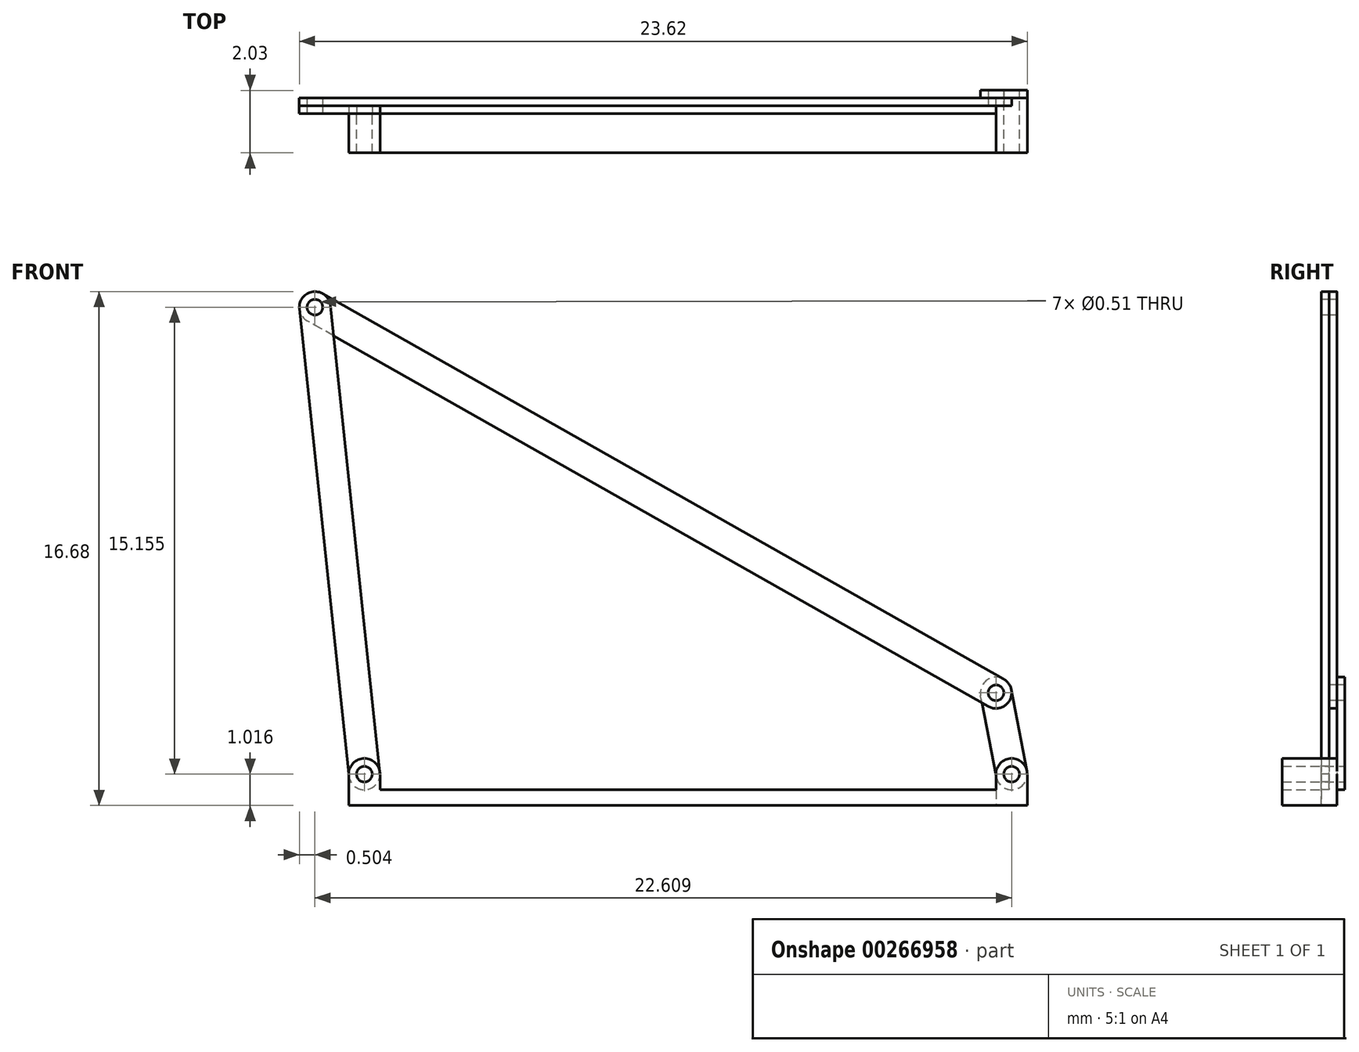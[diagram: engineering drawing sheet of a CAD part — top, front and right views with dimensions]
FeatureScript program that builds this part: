
annotation { "Feature Type Name" : "Feature", "Feature Type Description" : "" }
export const myFeature = defineFeature(function(context is Context, id is Id, definition is map)
    precondition{}
    {
        {
            var Q0;
            Q0=qCreatedBy(makeId("Front.planeOp"),FACE);
            var sketch = newSketch(context, id + "F0", { "sketchPlane" : qUnion([Q0])});
            skLineSegment(sketch, "E0.bottom", {"start": v(0, 0) * mm, "end": v(22.02, 0) * mm});
            skLineSegment(sketch, "E0.top", {"start": v(0, 0.5) * mm, "end": v(22.02, 0.5) * mm});
            skLineSegment(sketch, "E0.left", {"start": v(0, 0) * mm, "end": v(0, 0.5) * mm});
            skLineSegment(sketch, "E0.right", {"start": v(22.02, 0) * mm, "end": v(22.02, 0.5) * mm});
            skArc(sketch, "E1", {"start": v(1.02, 1.02) * mm, "mid": v(0.5, 1.52) * mm, "end": v(0, 1.02) * mm});
            skCircle(sketch, "E2", {"center": v(0.5, 1.02) * mm, "radius": 0.25 * mm});
            skLineSegment(sketch, "E3", {"start": v(0, 0.5) * mm, "end": v(0, 1.36) * mm});
            skLineSegment(sketch, "E4", {"start": v(1.02, 1.02) * mm, "end": v(1.02, 0.5) * mm});
            skArc(sketch, "E5", {"start": v(22.02, 1.02) * mm, "mid": v(21.51, 1.52) * mm, "end": v(21, 1.02) * mm});
            skCircle(sketch, "E6", {"center": v(21.51, 1.02) * mm, "radius": 0.25 * mm});
            skLineSegment(sketch, "E7", {"start": v(22.02, 1.02) * mm, "end": v(22.02, 0.5) * mm});
            skLineSegment(sketch, "E8", {"start": v(21, 1.02) * mm, "end": v(21, 0.5) * mm});
            skLineSegment(sketch, "E9", {"start": v(2.53, 4.51) * mm, "end": v(23.12, 16.17) * mm, "construction": true});
            skLineSegment(sketch, "E10", {"start": v(23.12, 16.17) * mm, "end": v(21.51, 1.02) * mm, "construction": true});
            skLineSegment(sketch, "E11", {"start": v(0.5, 1.02) * mm, "end": v(2.53, 4.51) * mm, "construction": true});
            skSolve(sketch);
        }
        {
            var Q0;
            {var subQ3=sQuery(id+"F0.wireOp",EDGE,"E1");Q0=makeQuery(id+"F0.imprint","IMPRINT",FACE,{"disambiguationData":[TD([[makeQuery(id+"F0.imprint","IMPRINT",EDGE,{"derivedFrom":subQ3}),1.0]])]});}
            var Q1;
            Q1=makeQuery(id+"F0.imprint","IMPRINT",FACE,{"disambiguationData":[TD([[makeQuery(id+"F0.imprint","IMPRINT",EDGE,{"derivedFrom":sQuery(id+"F0.wireOp",EDGE,"E0.bottom")}),1.0]])]});
            var Q2;
            Q2=makeQuery(id+"F0.imprint","IMPRINT",FACE,{"disambiguationData":[TD([[makeQuery(id+"F0.imprint","IMPRINT",EDGE,{"derivedFrom":sQuery(id+"F0.wireOp",EDGE,"E5")}),1.0]])]});
            extrude(context, id + "F1", {"entities" : qUnion([Q0, Q1, Q2]), "depth" : 1.27 * mm});
        }
        {
            var Q0;
            Q0=makeQuery(id+"F1.opExtrude","CAP_FACE",FACE,{"disambiguationData":[OSD([sQuery(id+"F0.wireOp",EDGE,"E0.bottom"),sQuery(id+"F0.wireOp",EDGE,"E0.top"),sQuery(id+"F0.wireOp",EDGE,"E0.left"),sQuery(id+"F0.wireOp",EDGE,"E0.right"),sQuery(id+"F0.wireOp",EDGE,"E1"),sQuery(id+"F0.wireOp",EDGE,"E2"),sQuery(id+"F0.wireOp",EDGE,"E3"),sQuery(id+"F0.wireOp",EDGE,"E4"),sQuery(id+"F0.wireOp",EDGE,"E5"),sQuery(id+"F0.wireOp",EDGE,"E6"),sQuery(id+"F0.wireOp",EDGE,"E7"),sQuery(id+"F0.wireOp",EDGE,"E8")])],"isStart":true});
            var sketch = newSketch(context, id + "F2", { "sketchPlane" : qUnion([Q0])});
            skCircle(sketch, "E12.0", {"center": v(-0.5, 1.02) * mm, "radius": 0.25 * mm});
            skCircle(sketch, "E13", {"center": v(-0.5, 1.02) * mm, "radius": 0.5 * mm});
            skLineSegment(sketch, "E14", {"start": v(-0.5, 1.02) * mm, "end": v(1.1, 16.17) * mm, "construction": true});
            skCircle(sketch, "E15", {"center": v(1.1, 16.17) * mm, "radius": 0.5 * mm});
            skLineSegment(sketch, "E16", {"start": v(0.6, 16.22) * mm, "end": v(-1.01, 1.07) * mm});
            skLineSegment(sketch, "E17", {"start": v(1.6, 16.12) * mm, "end": v(0, 1.02) * mm});
            skCircle(sketch, "E18", {"center": v(1.1, 16.17) * mm, "radius": 0.25 * mm});
            skSolve(sketch);
        }
        {
            var Q0;
            Q0 = qSketchRegion(id + "F2", true);
            extrude(context, id + "F3", {"entities" : qUnion([Q0]), "depth" : 0.25 * mm});
        }
        {
            var Q0;
            Q0=makeQuery(id+"F3.opExtrude","CAP_FACE",FACE,{"disambiguationData":[OSD([sQuery(id+"F2.wireOp",EDGE,"E12.0"),sQuery(id+"F2.wireOp",EDGE,"E13"),sQuery(id+"F2.wireOp",EDGE,"E15"),sQuery(id+"F2.wireOp",EDGE,"E16"),sQuery(id+"F2.wireOp",EDGE,"E17"),sQuery(id+"F2.wireOp",EDGE,"E18")])],"isStart":false});
            var sketch = newSketch(context, id + "F4", { "sketchPlane" : qUnion([Q0])});
            skCircle(sketch, "E19.0", {"center": v(1.1, 16.17) * mm, "radius": 0.25 * mm});
            skCircle(sketch, "E20", {"center": v(1.1, 16.17) * mm, "radius": 0.5 * mm});
            skLineSegment(sketch, "E21", {"start": v(1.1, 16.17) * mm, "end": v(-21, 3.66) * mm, "construction": true});
            skCircle(sketch, "E22", {"center": v(-21, 3.66) * mm, "radius": 0.5 * mm});
            skCircle(sketch, "E23", {"center": v(-21, 3.66) * mm, "radius": 0.25 * mm});
            skLineSegment(sketch, "E24", {"start": v(-21.26, 4.1) * mm, "end": v(0.85, 16.61) * mm});
            skLineSegment(sketch, "E25", {"start": v(-20.76, 3.21) * mm, "end": v(1.35, 15.73) * mm});
            skSolve(sketch);
        }
        {
            var Q0;
            Q0 = qSketchRegion(id + "F4", true);
            extrude(context, id + "F5", {"entities" : qUnion([Q0]), "depth" : 0.25 * mm});
        }
        {
            var Q0;
            Q0=makeQuery(id+"F5.opExtrude","CAP_FACE",FACE,{"disambiguationData":[OSD([sQuery(id+"F4.wireOp",EDGE,"E19.0"),sQuery(id+"F4.wireOp",EDGE,"E20"),sQuery(id+"F4.wireOp",EDGE,"E22"),sQuery(id+"F4.wireOp",EDGE,"E23"),sQuery(id+"F4.wireOp",EDGE,"E24"),sQuery(id+"F4.wireOp",EDGE,"E25")])],"isStart":false});
            var sketch = newSketch(context, id + "F6", { "sketchPlane" : qUnion([Q0])});
            skCircle(sketch, "E26.0", {"center": v(-21, 3.66) * mm, "radius": 0.25 * mm});
            skCircle(sketch, "E27.0", {"center": v(-21.51, 1.02) * mm, "radius": 0.25 * mm});
            skCircle(sketch, "E28", {"center": v(-21, 3.66) * mm, "radius": 0.5 * mm});
            skCircle(sketch, "E29", {"center": v(-21.51, 1.02) * mm, "radius": 0.5 * mm});
            skLineSegment(sketch, "E30", {"start": v(-22.01, 1.11) * mm, "end": v(-21.5, 3.75) * mm});
            skLineSegment(sketch, "E31", {"start": v(-21.01, 0.92) * mm, "end": v(-20.5, 3.56) * mm});
            skSolve(sketch);
        }
        {
            var Q0;
            Q0 = qSketchRegion(id + "F6", true);
            extrude(context, id + "F7", {"entities" : qUnion([Q0]), "depth" : 0.25 * mm});
        }
        {
            var Q0;
            Q0=makeQuery(id+"F1.opExtrude","CAP_FACE",FACE,{"disambiguationData":[OSD([sQuery(id+"F0.wireOp",EDGE,"E0.bottom"),sQuery(id+"F0.wireOp",EDGE,"E0.top"),sQuery(id+"F0.wireOp",EDGE,"E0.left"),sQuery(id+"F0.wireOp",EDGE,"E0.right"),sQuery(id+"F0.wireOp",EDGE,"E1"),sQuery(id+"F0.wireOp",EDGE,"E2"),sQuery(id+"F0.wireOp",EDGE,"E3"),sQuery(id+"F0.wireOp",EDGE,"E4"),sQuery(id+"F0.wireOp",EDGE,"E5"),sQuery(id+"F0.wireOp",EDGE,"E6"),sQuery(id+"F0.wireOp",EDGE,"E7"),sQuery(id+"F0.wireOp",EDGE,"E8")])],"isStart":true});
            var sketch = newSketch(context, id + "F8", { "sketchPlane" : qUnion([Q0])});
            skArc(sketch, "E32.0", {"start": v(-22.02, 1.02) * mm, "mid": v(-21.51, 1.52) * mm, "end": v(-21, 1.02) * mm});
            skCircle(sketch, "E33.0", {"center": v(-21.51, 1.02) * mm, "radius": 0.25 * mm});
            skArc(sketch, "E34.0", {"start": v(-22.01, 1.11) * mm, "mid": v(-21.6, 0.52) * mm, "end": v(-21.01, 0.92) * mm});
            skLineSegment(sketch, "E35.0", {"start": v(-21, 1.02) * mm, "end": v(-21, 0.5) * mm});
            skLineSegment(sketch, "E36.0", {"start": v(-22.02, 1.02) * mm, "end": v(-22.02, 0.5) * mm});
            skLineSegment(sketch, "E37.0", {"start": v(-22.02, 0) * mm, "end": v(-22.02, 0.5) * mm});
            skLineSegment(sketch, "E38", {"start": v(-21, 0.5) * mm, "end": v(-21, 0) * mm});
            skLineSegment(sketch, "E39.0", {"start": v(-21, 0) * mm, "end": v(-22.02, 0) * mm});
            skPoint(sketch, "E40.orphan", {"position": v(0, 0) * mm});
            skSolve(sketch);
        }
        {
            var Q0;
            Q0 = qSketchRegion(id + "F8", true);
            extrude(context, id + "F9", {"entities" : qUnion([Q0]), "operationType" : NewBodyOperationType.ADD, "depth" : 0.5 * mm});
        }
    });
